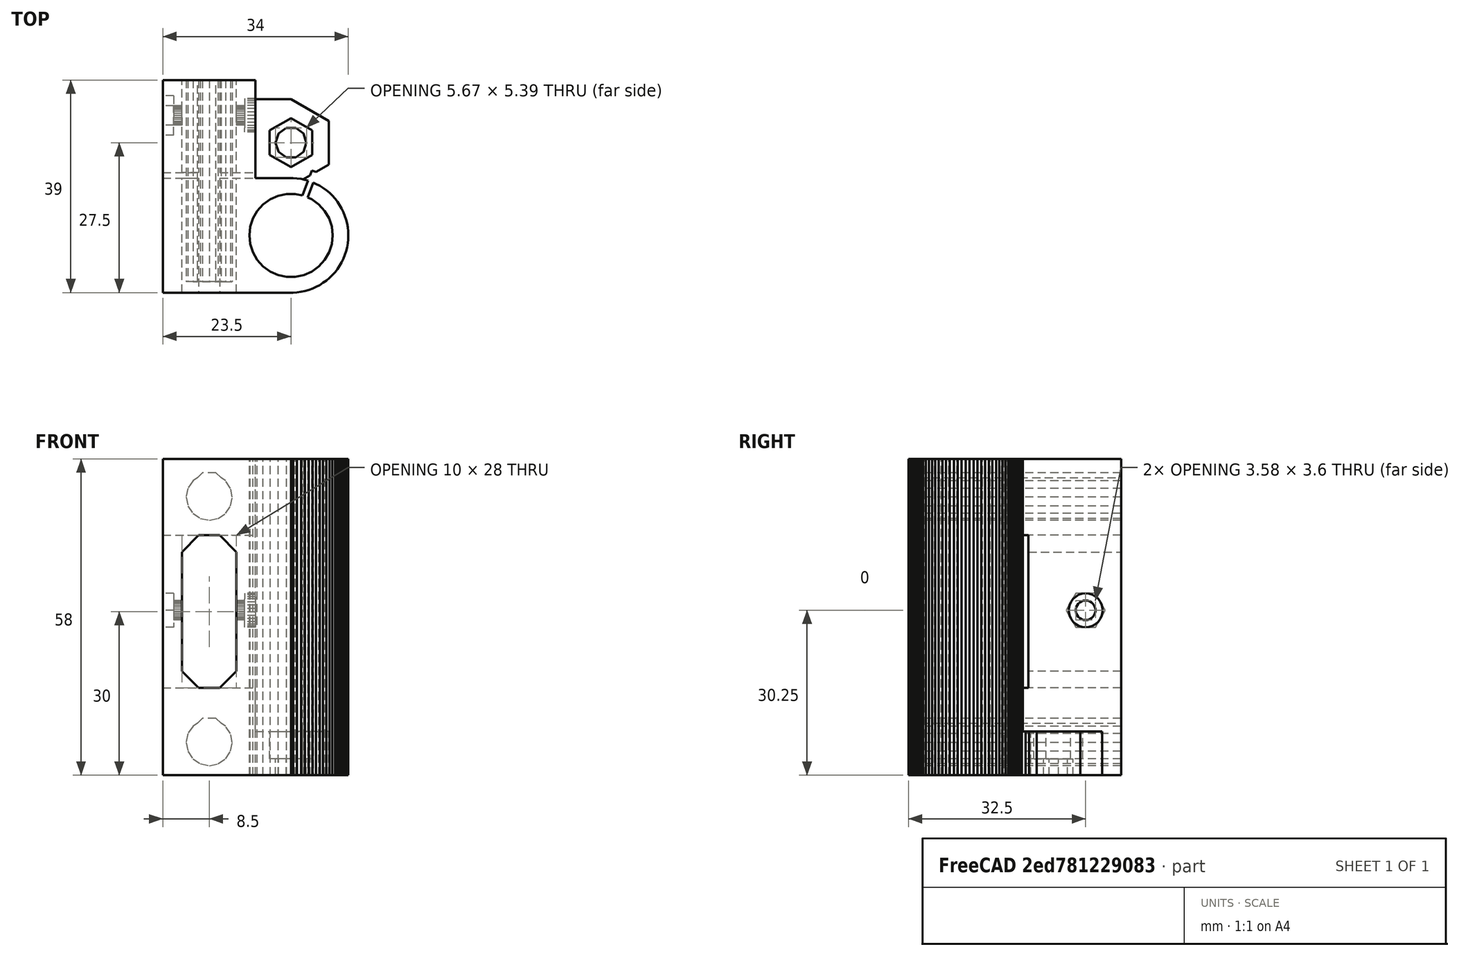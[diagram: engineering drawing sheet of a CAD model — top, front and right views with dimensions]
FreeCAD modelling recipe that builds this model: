
FCSTD DOCUMENT  (FreeCAD 0.15R4368 (Git))
Label: x-end-idlar
License: CC-BY 3.0
LicenseURL: http://creativecommons.org/licenses/by/3.0/
objects: Part::Box×14, Part::Prism×10, Part::Fuse×5, Part::MultiFuse×4, Part::Cut×4, Part::Mirroring×1, Part::Feature×1
note: 39 computed .brp shape members not serialized (recipe doc carries the construction recipe); baked Part::Feature solids carry a one-line shape summary decoded from their .brp

FEATURE [Part::Box] cube
  Height = 58
  Length = 17
  Placement = pos=(-23.5,-28.5,0) rot=(0,0,1;0rad)
  Width = 39
FEATURE [Part::Box] cube001
  Height = 58
  Length = 14.5
  Placement = pos=(-14.5,-10.5,0) rot=(0,0,1;0rad)
  Width = 21
FEATURE [Part::Prism] prism
  Circumradius = 10.5
  Height = 58
  Polygon = 90
FEATURE [Part::Fuse] Group
  Base = -> cube001
  Tool = -> prism
FEATURE [Part::Box] cube002
  Height = 8
  Length = 8
  Placement = pos=(-8,-25,0) rot=(0,0,1;0rad)
  Width = 16
FEATURE [Part::Prism] prism001
  Circumradius = 8
  Height = 8
  Placement = pos=(0,-17,0) rot=(0,0,1;0.523599rad)
  Polygon = 6
FEATURE [Part::MultiFuse] Group001
  Shapes = -> [cube,Group,cube002,prism001]
FEATURE [Part::Prism] prism002
  Circumradius = 7.64131
  Height = 62
  Placement = pos=(0,0,-1) rot=(0,0,1;0rad)
  Polygon = 30
FEATURE [Part::Box] cube003
  Height = 62
  Length = 6
  Placement = pos=(1.75328,-6.27901,-1) rot=(0,0,-1;1.22173rad)
  Width = 1
FEATURE [Part::Fuse] Group002
  Base = -> prism002
  Tool = -> cube003
FEATURE [Part::Box] cube004
  Height = 28
  Length = 20
  Placement = pos=(-24,-11.5,16) rot=(0,0,1;0rad)
  Width = 1
FEATURE [Part::Box] cube005
  Height = 28
  Length = 10
  Placement = pos=(-19,-33,16) rot=(0,0,1;0rad)
  Width = 46
FEATURE [Part::Box] cube006
  Height = 28
  Length = 10
  Placement = pos=(-27.435,-33,46.636) rot=(0,1,0;0.785398rad)
  Width = 46
FEATURE [Part::Box] cube007
  Height = 28
  Length = 10
  Placement = pos=(-7.63604,-33,39.565) rot=(0,-1,0;0.785398rad)
  Width = 46
FEATURE [Part::Box] cube008
  Height = 28
  Length = 10
  Placement = pos=(-27.435,-33,0.636039) rot=(0,1,0;0.785398rad)
  Width = 46
FEATURE [Part::Box] cube009
  Height = 28
  Length = 10
  Placement = pos=(-7.63604,-33,-6.43503) rot=(0,-1,0;0.785398rad)
  Width = 46
FEATURE [Part::MultiFuse] union
  Shapes = -> [cube006,cube007,cube008,cube009]
FEATURE [Part::Cut] difference
  Base = -> cube005
  Tool = -> union
FEATURE [Part::Fuse] Matrix_Union
  Base = -> cube004
  Placement = pos=(-1,0,0) rot=(0,0,1;0rad)
  Tool = -> difference
FEATURE [Part::Prism] prism003
  Circumradius = 4.22934
  Height = 50
  Polygon = 16
FEATURE [Part::Box] cube010
  Height = 50
  Length = 4.05
  Placement = pos=(0,-5.70589,0) rot=(0,0,1;0.785398rad)
  Width = 4.05
FEATURE [Part::Box] cube011
  Height = 50
  Length = 8.1
  Placement = pos=(-4.05,-8.5,0) rot=(0,0,1;0rad)
  Width = 4.05
FEATURE [Part::Cut] difference001
  Base = -> cube010
  Tool = -> cube011
FEATURE [Part::Fuse] Group003
  Base = -> prism003
  Placement = pos=(-15,-41.5,6) rot=(-1,0,0;1.5708rad)
  Tool = -> difference001
FEATURE [Part::Prism] prism004
  Circumradius = 4.22934
  Height = 50
  Polygon = 16
FEATURE [Part::Box] cube012
  Height = 50
  Length = 4.05
  Placement = pos=(0,-5.70589,0) rot=(0,0,1;0.785398rad)
  Width = 4.05
FEATURE [Part::Box] cube013
  Height = 50
  Length = 8.1
  Placement = pos=(-4.05,-8.5,0) rot=(0,0,1;0rad)
  Width = 4.05
FEATURE [Part::Cut] difference002
  Base = -> cube012
  Tool = -> cube013
FEATURE [Part::Fuse] Group004
  Base = -> prism004
  Placement = pos=(-15,-41.5,51) rot=(-1,0,0;1.5708rad)
  Tool = -> difference002
FEATURE [Part::Prism] prism005
  Circumradius = 2.8338
  Height = 4
  Placement = pos=(0,-17,-0.5) rot=(0,0,1;0rad)
  Polygon = 10
FEATURE [Part::Prism] prism006
  Circumradius = 4.5
  Height = 10
  Placement = pos=(0,-17,3) rot=(0,0,1;0.523599rad)
  Polygon = 6
FEATURE [Part::MultiFuse] Group005
  Shapes = -> [Group002,Matrix_Union,Group003,Group004,prism005,prism006]
FEATURE [Part::Prism] prism007
  Circumradius = 1.8
  Height = 80
  Placement = pos=(0,-22,30.25) rot=(0,-1,0;1.5708rad)
  Polygon = 30
FEATURE [Part::Prism] prism008
  Circumradius = 3.1
  Height = 10
  Placement = pos=(1.5,-22,30.25) rot=(0,-1,0;1.5708rad)
  Polygon = 30
FEATURE [Part::Prism] prism009
  Circumradius = 3.6
  Height = 80
  Placement = pos=(-21.5,-22,30.25) rot=(-0.250563,-0.935113,0.250563;1.63783rad)
  Polygon = 6
FEATURE [Part::MultiFuse] Group006
  Shapes = -> [Group005,prism007,prism008,prism009]
FEATURE [Part::Cut] difference003
  Base = -> Group001
  Tool = -> Group006
FEATURE [Part::Mirroring] mirr_difference003  label="mirrored difference003"
  Base = (0,0,0)
  Normal = (0,1,0)
  Source = -> difference003
FEATURE [Part::Feature] mirr_difference003001  label="XidlerPrusa"
  shape: bbox 34 x 39 x 58 mm, 262 faces (baked)
